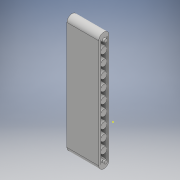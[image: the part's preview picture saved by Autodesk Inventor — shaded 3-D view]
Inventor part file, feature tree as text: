
AUTODESK INVENTOR PART (.ipt)
format: ipt  version: 2018 (Build 220112000, 112)  size: 171,520 bytes
history: native  units: mm
features: sketch x6, extrude x4
ambient origin geometry x8: Origin, YZ Plane, XZ Plane, XY Plane, X Axis, Y Axis, Z Axis, Center Point
bodies: Solid1 (feature_tree)
feature tree (10):
  extrude  "Extrusion1"  Depth=30.0mm
  extrude  "Extrusion2"  Depth=500.0mm TaperAngle=0.0deg
  sketch  "Sketch3"  dims[d10=1700.0mm d11=100.0mm]
  sketch  "Sketch4"  dims[d12=30.0mm d13=500.0mm d14=0.0mm]
  sketch  "Sketch5"  dims[d17=170.0mm]
  extrude  "Extrusion3"  Depth=100.0mm
  extrude  "Extrusion4"  Depth=500.0mm TaperAngle=0.0deg
  sketch  "Sketch1"  dims[d5=1700.0mm d6=30.0mm]
  sketch  "Sketch2"  dims[d7=30.0mm d8=500.0mm d9=0.0mm]
  sketch  "Sketch6"  dims[d18=170.0mm d19=170.0mm d20=170.0mm d21=170.0mm d23=170.0mm d24=170.0mm d25=170.0mm d26=170.0mm d27=170.0mm d28=0.0mm d29=500.0mm d30=0.0mm d31=50.0mm d32=50.0mm d33=30.0mm d34=530.0mm d35=0.0mm d36=0.0mm]
